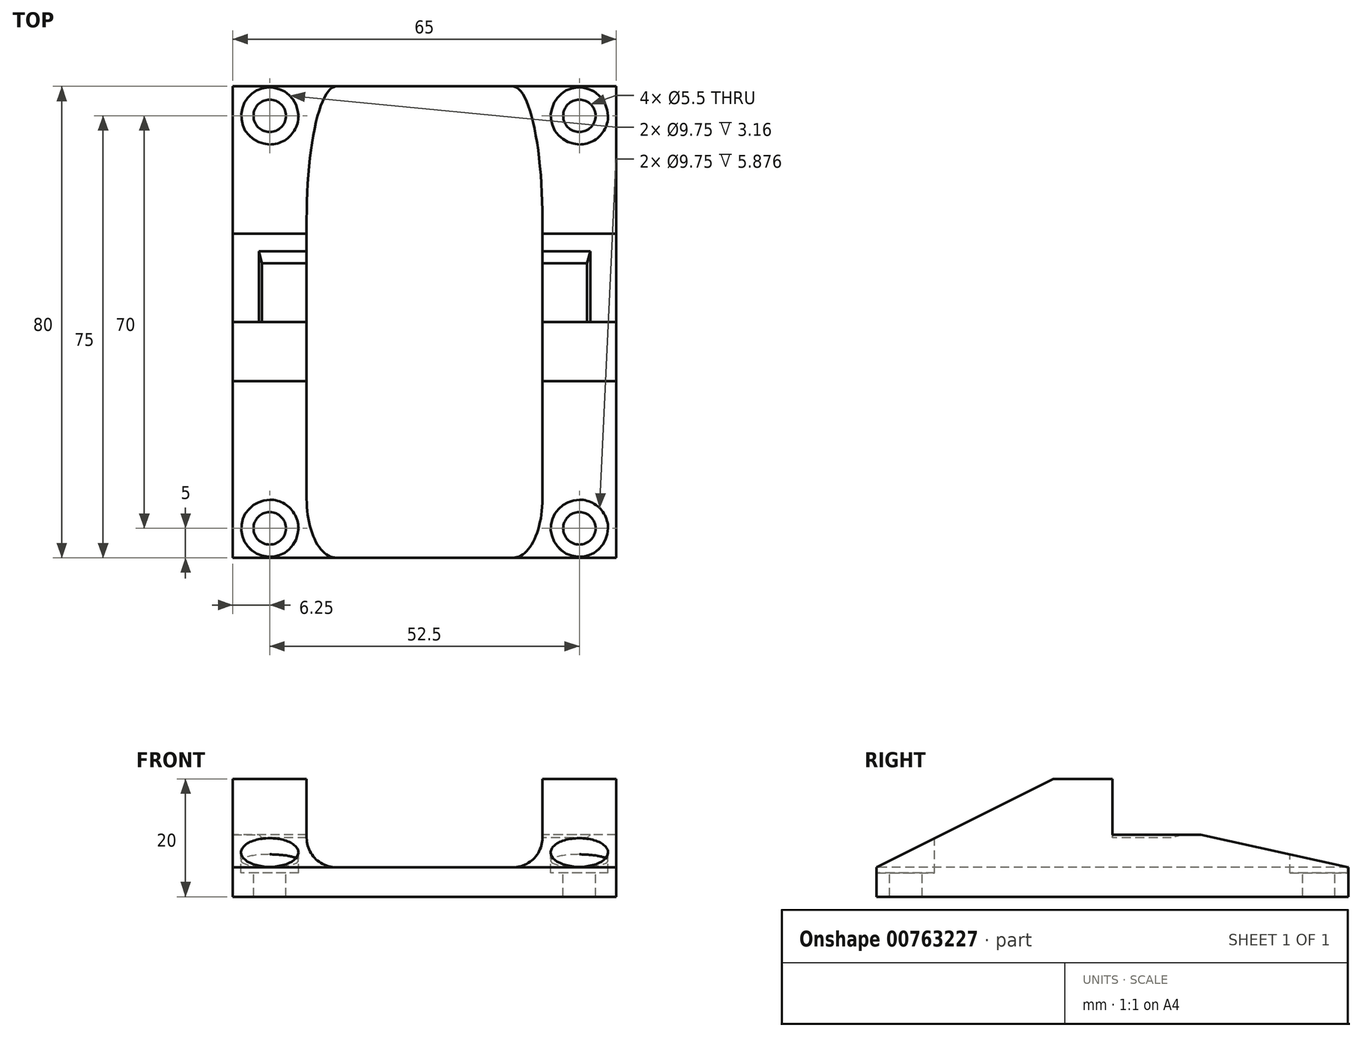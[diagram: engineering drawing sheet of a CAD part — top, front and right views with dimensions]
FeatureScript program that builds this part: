
annotation { "Feature Type Name" : "Feature", "Feature Type Description" : "" }
export const myFeature = defineFeature(function(context is Context, id is Id, definition is map)
    precondition{}
    {
        {
            var Q0;
            Q0=qCreatedBy(makeId("Right.planeOp"),FACE);
            var sketch = newSketch(context, id + "F0", { "sketchPlane" : qUnion([Q0])});
            skLineSegment(sketch, "E0", {"start": v(0, 20) * mm, "end": v(0, 10) * mm});
            skLineSegment(sketch, "E1", {"start": v(0, 10) * mm, "end": v(10, 10) * mm});
            skLineSegment(sketch, "E2", {"start": v(10, 10) * mm, "end": v(12, 10.54) * mm});
            skLineSegment(sketch, "E3", {"start": v(12, 10.54) * mm, "end": v(15, 10.54) * mm});
            skLineSegment(sketch, "E4", {"start": v(40, 0) * mm, "end": v(-40, 0) * mm});
            skLineSegment(sketch, "E5", {"start": v(-10, 20) * mm, "end": v(0, 20) * mm});
            skLineSegment(sketch, "E6", {"start": v(-40, 0) * mm, "end": v(-40, 5) * mm});
            skLineSegment(sketch, "E7", {"start": v(-40, 5) * mm, "end": v(-10, 20) * mm});
            skLineSegment(sketch, "E8", {"start": v(40, 0) * mm, "end": v(40, 5) * mm});
            skLineSegment(sketch, "E9", {"start": v(40, 5) * mm, "end": v(15, 10.54) * mm});
            skPoint(sketch, "E10", {"position": v(0, 0) * mm});
            skSolve(sketch);
        }
        {
            var Q0;
            Q0=qSketchRegion(id+"F0",true);
            extrude(context, id + "F1", {"entities" : qUnion([Q0]), "endBound" : BoundingType.SYMMETRIC, "depth" : 65 * mm, "offsetDistance" : 25 * mm});
        }
        {
            var Q0;
            Q0=qCreatedBy(makeId("Front.planeOp"),FACE);
            var sketch = newSketch(context, id + "F2", { "sketchPlane" : qUnion([Q0])});
            skLineSegment(sketch, "E11.bottom", {"start": v(20, 5) * mm, "end": v(-20, 5) * mm});
            skLineSegment(sketch, "E11.top", {"start": v(20, 20) * mm, "end": v(-20, 20) * mm});
            skLineSegment(sketch, "E11.left", {"start": v(20, 5) * mm, "end": v(20, 20) * mm});
            skLineSegment(sketch, "E11.right", {"start": v(-20, 5) * mm, "end": v(-20, 20) * mm});
            skPoint(sketch, "E11.middle", {"position": v(0, 12.5) * mm});
            skSolve(sketch);
        }
        {
            var Q0;
            Q0=qSketchRegion(id+"F2",true);
            extrude(context, id + "F3", {"entities" : qUnion([Q0]), "operationType" : NewBodyOperationType.REMOVE, "endBound" : BoundingType.THROUGH_ALL, "oppositeDirection" : true, "depth" : 25 * mm, "offsetDistance" : 25 * mm, "hasSecondDirection" : true, "secondDirectionBound" : SecondDirectionBoundingType.THROUGH_ALL, "secondDirectionOppositeDirection" : false, "secondDirectionDepth" : 25 * mm});
        }
        {
            var Q0;
            Q0=makeQuery(id+"F3.boolean.opBoolean","COPY",EDGE,{"derivedFrom":makeQuery(id+"F3.opExtrude","SWEPT_EDGE",EDGE,{"disambiguationData":[OSD([sQuery(id+"F2.wireOp",EDGE,"E11.bottom"),sQuery(id+"F2.wireOp",EDGE,"E11.left")])]})});
            var Q1;
            Q1=makeQuery(id+"F3.boolean.opBoolean","COPY",EDGE,{"derivedFrom":makeQuery(id+"F3.opExtrude","SWEPT_EDGE",EDGE,{"disambiguationData":[OSD([sQuery(id+"F2.wireOp",EDGE,"E11.bottom"),sQuery(id+"F2.wireOp",EDGE,"E11.right")])]})});
            fillet(context, id + "F4", {"entities" : qUnion([Q0, Q1]), "radius" : 5 * mm, "tangentPropagation" : true, "allowEdgeOverflow" : false});
        }
        {
            var Q0;
            {var subQ2=sQuery(id+"F0.wireOp",EDGE,"E1");Q0=makeQuery(id+"F3.boolean.opBoolean","SPLIT",FACE,{"disambiguationData":[TD([makeQuery(id+"F3.opExtrude","SWEPT_FACE",FACE,{"disambiguationData":[OSD([sQuery(id+"F2.wireOp",EDGE,"E11.right")])]})])],"derivedFrom":makeQuery(id+"F1.opExtrude","SWEPT_FACE",FACE,{"disambiguationData":[OSD([subQ2])]})});}
            var sketch = newSketch(context, id + "F5", { "sketchPlane" : qUnion([Q0])});
            skLineSegment(sketch, "E12.bottom", {"start": v(-26.25, 35) * mm, "end": v(26.25, 35) * mm, "construction": true});
            skLineSegment(sketch, "E12.top", {"start": v(-26.25, -35) * mm, "end": v(26.25, -35) * mm, "construction": true});
            skLineSegment(sketch, "E12.left", {"start": v(-26.25, 35) * mm, "end": v(-26.25, -35) * mm, "construction": true});
            skLineSegment(sketch, "E12.right", {"start": v(26.25, 35) * mm, "end": v(26.25, -35) * mm, "construction": true});
            skPoint(sketch, "E12.middle", {"position": v(0, 0) * mm});
            skPoint(sketch, "E13", {"position": v(-26.25, 35) * mm});
            skPoint(sketch, "E14", {"position": v(26.25, 35) * mm});
            skPoint(sketch, "E15", {"position": v(26.25, -35) * mm});
            skPoint(sketch, "E16", {"position": v(-26.25, -35) * mm});
            skSolve(sketch);
        }
        {
            var Q0;
            Q0=sQuery(id+"F5.wireOp",VERTEX,"E13");
            var Q1;
            Q1=sQuery(id+"F5.wireOp",VERTEX,"E14");
            var Q2;
            Q2=sQuery(id+"F5.wireOp",VERTEX,"E16");
            var Q3;
            Q3=sQuery(id+"F5.wireOp",VERTEX,"E15");
            var Q4;
            Q4=makeQuery(id+"F1.opExtrude","SWEPT_BODY",BODY,{"disambiguationData":[OSD([sQuery(id+"F0.wireOp",EDGE,"E0"),sQuery(id+"F0.wireOp",EDGE,"E1"),sQuery(id+"F0.wireOp",EDGE,"E2"),sQuery(id+"F0.wireOp",EDGE,"E3"),sQuery(id+"F0.wireOp",EDGE,"E4"),sQuery(id+"F0.wireOp",EDGE,"E5"),sQuery(id+"F0.wireOp",EDGE,"E6"),sQuery(id+"F0.wireOp",EDGE,"E7"),sQuery(id+"F0.wireOp",EDGE,"E8"),sQuery(id+"F0.wireOp",EDGE,"E9")])]});
            hole(context, id + "F6", {"style" : HoleStyle.C_BORE, "endStyle" : HoleEndStyle.THROUGH, "holeDiameter" : 5.5 * mm, "cBoreDiameter" : 9.75 * mm, "cBoreDepth" : 1 * mm, "majorDiameter" : 5 * mm, "isTappedThrough" : true, "tappedDepth" : 12 * mm, "tapClearance" : 3, "locations" : qUnion([Q0, Q1, Q2, Q3]), "scope" : qUnion([Q4])});
        }
        {
            var Q0;
            {var subQ2=sQuery(id+"F0.wireOp",EDGE,"E1");Q0=makeQuery(id+"F3.boolean.opBoolean","SPLIT",FACE,{"disambiguationData":[TD([makeQuery(id+"F3.opExtrude","SWEPT_FACE",FACE,{"disambiguationData":[OSD([sQuery(id+"F2.wireOp",EDGE,"E11.left")])]})])],"derivedFrom":makeQuery(id+"F1.opExtrude","SWEPT_FACE",FACE,{"disambiguationData":[OSD([subQ2])]})});}
            var sketch = newSketch(context, id + "F7", { "sketchPlane" : qUnion([Q0])});
            skLineSegment(sketch, "E17.bottom", {"start": v(-32.5, 0) * mm, "end": v(-27.5, 0) * mm});
            skLineSegment(sketch, "E17.top", {"start": v(-32.5, 12) * mm, "end": v(-27.5, 12) * mm});
            skLineSegment(sketch, "E17.left", {"start": v(-32.5, 0) * mm, "end": v(-32.5, 12) * mm});
            skLineSegment(sketch, "E17.right", {"start": v(-27.5, 0) * mm, "end": v(-27.5, 12) * mm});
            skLineSegment(sketch, "E18", {"start": v(0, 0) * mm, "end": v(0, 44.26) * mm, "construction": true});
            skLineSegment(sketch, "E19.MirrorCS", {"start": v(32.5, 0) * mm, "end": v(27.5, 0) * mm});
            skLineSegment(sketch, "E20.MirrorCS", {"start": v(32.5, 12) * mm, "end": v(27.5, 12) * mm});
            skLineSegment(sketch, "E21.MirrorCS", {"start": v(32.5, 0) * mm, "end": v(32.5, 12) * mm});
            skLineSegment(sketch, "E22.MirrorCS", {"start": v(27.5, 0) * mm, "end": v(27.5, 12) * mm});
            skSolve(sketch);
        }
        {
            var Q0;
            Q0=qSketchRegion(id+"F7",true);
            var Q1;
            {var subQ1=sQuery(id+"F0.wireOp",EDGE,"E3");Q1=makeQuery(id+"F3.boolean.opBoolean","SPLIT",FACE,{"disambiguationData":[TD([makeQuery(id+"F3.opExtrude","SWEPT_FACE",FACE,{"disambiguationData":[OSD([sQuery(id+"F2.wireOp",EDGE,"E11.left")])]})])],"derivedFrom":makeQuery(id+"F1.opExtrude","SWEPT_FACE",FACE,{"disambiguationData":[OSD([subQ1])]})});}
            extrude(context, id + "F8", {"entities" : qUnion([Q0]), "operationType" : NewBodyOperationType.ADD, "endBound" : BoundingType.UP_TO_SURFACE, "depth" : 25 * mm, "endBoundEntityFace" : qUnion([Q1]), "offsetDistance" : 25 * mm});
        }
        {
            var Q0;
            Q0=makeQuery(id+"F8.opExtrude","CAP_EDGE",EDGE,{"disambiguationData":[OSD([sQuery(id+"F7.wireOp",EDGE,"E22.MirrorCS")])],"isStart":false});
            var Q1;
            Q1=makeQuery(id+"F8.opExtrude","CAP_EDGE",EDGE,{"disambiguationData":[OSD([sQuery(id+"F7.wireOp",EDGE,"E17.right")])],"isStart":false});
            chamfer(context, id + "F9", {"entities" : qUnion([Q0, Q1]), "chamferType" : ChamferType.OFFSET_ANGLE, "width" : 0.6 * mm, "oppositeDirection" : true, "angle" : 45 * degree, "tangentPropagation" : true});
        }
        {
            var Q0;
            {var subQ2=sQuery(id+"F0.wireOp",EDGE,"E0");Q0=makeQuery(id+"F3.boolean.opBoolean","SPLIT",FACE,{"disambiguationData":[TD([makeQuery(id+"F3.opExtrude","SWEPT_FACE",FACE,{"disambiguationData":[OSD([sQuery(id+"F2.wireOp",EDGE,"E11.left")])]})])],"derivedFrom":makeQuery(id+"F1.opExtrude","SWEPT_FACE",FACE,{"disambiguationData":[OSD([subQ2])]})});}
            var sketch = newSketch(context, id + "F10", { "sketchPlane" : qUnion([Q0])});
            skLineSegment(sketch, "E23", {"start": v(-20, 20) * mm, "end": v(20, 10) * mm, "construction": true});
            skPoint(sketch, "E24", {"position": v(0, 15) * mm});
            skSolve(sketch);
        }
    });
